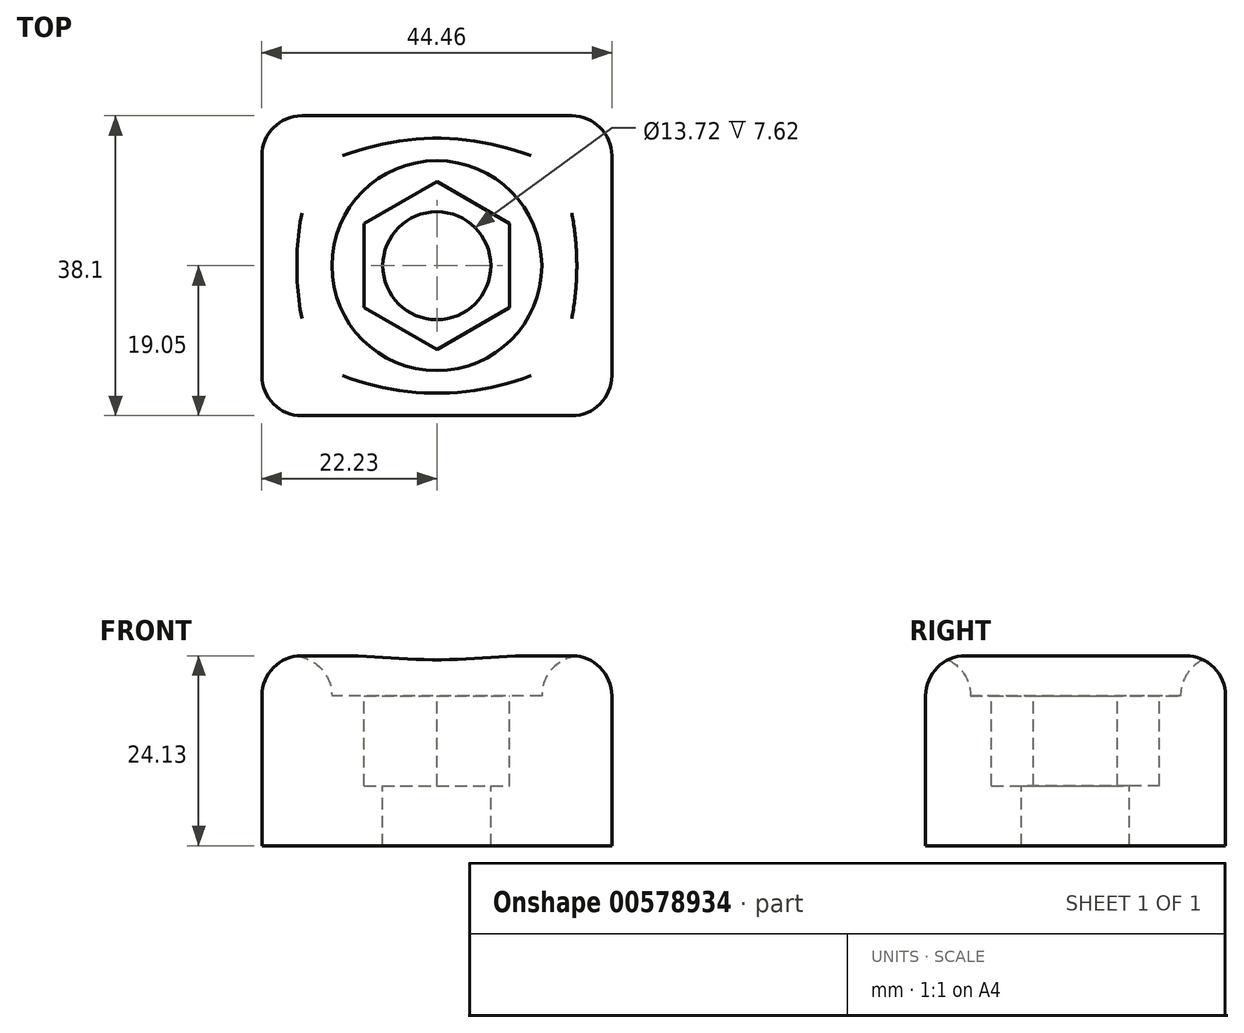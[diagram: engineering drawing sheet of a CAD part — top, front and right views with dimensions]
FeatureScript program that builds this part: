
annotation { "Feature Type Name" : "Feature", "Feature Type Description" : "" }
export const myFeature = defineFeature(function(context is Context, id is Id, definition is map)
    precondition{}
    {
        {
            var Q0;
            Q0=qCreatedBy(makeId("Top.planeOp"),FACE);
            var sketch = newSketch(context, id + "F0", { "sketchPlane" : qUnion([Q0])});
            skLineSegment(sketch, "E0.bottom", {"start": v(-22.23, 19.05) * mm, "end": v(22.23, 19.05) * mm});
            skLineSegment(sketch, "E0.top", {"start": v(-22.23, -19.05) * mm, "end": v(22.23, -19.05) * mm});
            skLineSegment(sketch, "E0.left", {"start": v(-22.23, 19.05) * mm, "end": v(-22.23, -19.05) * mm});
            skLineSegment(sketch, "E0.right", {"start": v(22.23, 19.05) * mm, "end": v(22.23, -19.05) * mm});
            skPoint(sketch, "E0.middle", {"position": v(0, 0) * mm});
            skSolve(sketch);
        }
        {
            var Q0;
            Q0=makeQuery(id+"F0.imprint","IMPRINT",FACE,{"disambiguationData":[TD([[makeQuery(id+"F0.imprint","IMPRINT",EDGE,{"derivedFrom":sQuery(id+"F0.wireOp",EDGE,"E0.bottom")}),-1.0]])]});
            extrude(context, id + "F1", {"entities" : qUnion([Q0]), "depth" : 16.5 * mm, "offsetDistance" : 25.4 * mm});
        }
        {
            var Q0;
            Q0=makeQuery(id+"F1.opExtrude","CAP_FACE",FACE,{"disambiguationData":[OSD([sQuery(id+"F0.wireOp",EDGE,"E0.bottom"),sQuery(id+"F0.wireOp",EDGE,"E0.top"),sQuery(id+"F0.wireOp",EDGE,"E0.left"),sQuery(id+"F0.wireOp",EDGE,"E0.right")])],"isStart":false});
            var sketch = newSketch(context, id + "F2", { "sketchPlane" : qUnion([Q0])});
            skCircle(sketch, "E1.cCircle", {"center": v(0, 0) * mm, "radius": 10.67 * mm, "construction": true});
            skLineSegment(sketch, "E1.0", {"start": v(0, 10.67) * mm, "end": v(9.24, 5.33) * mm});
            skLineSegment(sketch, "E1.1", {"start": v(9.24, 5.33) * mm, "end": v(9.24, -5.33) * mm});
            skLineSegment(sketch, "E1.2", {"start": v(9.24, -5.33) * mm, "end": v(0, -10.67) * mm});
            skLineSegment(sketch, "E1.3", {"start": v(0, -10.67) * mm, "end": v(-9.24, -5.33) * mm});
            skLineSegment(sketch, "E1.4", {"start": v(-9.24, -5.33) * mm, "end": v(-9.24, 5.33) * mm});
            skLineSegment(sketch, "E1.5", {"start": v(-9.24, 5.33) * mm, "end": v(0, 10.67) * mm});
            skSolve(sketch);
        }
        {
            var Q0;
            Q0=makeQuery(id+"F2.imprint","IMPRINT",FACE,{"disambiguationData":[TD([[makeQuery(id+"F2.imprint","IMPRINT",EDGE,{"derivedFrom":sQuery(id+"F2.wireOp",EDGE,"E1.0")}),-1.0]])]});
            extrude(context, id + "F3", {"entities" : qUnion([Q0]), "operationType" : NewBodyOperationType.REMOVE, "oppositeDirection" : true, "depth" : 25.4 * mm, "offsetDistance" : 25.4 * mm});
        }
        {
            var Q0;
            Q0=makeQuery(id+"F1.opExtrude","CAP_FACE",FACE,{"disambiguationData":[OSD([sQuery(id+"F0.wireOp",EDGE,"E0.bottom"),sQuery(id+"F0.wireOp",EDGE,"E0.top"),sQuery(id+"F0.wireOp",EDGE,"E0.left"),sQuery(id+"F0.wireOp",EDGE,"E0.right")])],"isStart":false});
            var sketch = newSketch(context, id + "F4", { "sketchPlane" : qUnion([Q0])});
            skCircle(sketch, "E2", {"center": v(0, 0) * mm, "radius": 13.34 * mm});
            skSolve(sketch);
        }
        {
            var Q0;
            Q0=makeQuery(id+"F4.imprint","IMPRINT",FACE,{"disambiguationData":[TD([[makeQuery(id+"F4.imprint","IMPRINT",EDGE,{"derivedFrom":sQuery(id+"F4.wireOp",EDGE,"E2")}),1.0]])]});
            extrude(context, id + "F5", {"entities" : qUnion([Q0]), "operationType" : NewBodyOperationType.REMOVE, "oppositeDirection" : true, "depth" : 5.08 * mm, "offsetDistance" : 25.4 * mm});
        }
        {
            var Q0;
            Q0=makeQuery(id+"F1.opExtrude","CAP_EDGE",EDGE,{"disambiguationData":[OSD([sQuery(id+"F0.wireOp",EDGE,"E0.bottom")])],"isStart":false});
            var Q1;
            Q1=makeQuery(id+"F1.opExtrude","CAP_EDGE",EDGE,{"disambiguationData":[OSD([sQuery(id+"F0.wireOp",EDGE,"E0.right")])],"isStart":false});
            var Q2;
            Q2=makeQuery(id+"F1.opExtrude","CAP_FACE",FACE,{"disambiguationData":[OSD([sQuery(id+"F0.wireOp",EDGE,"E0.bottom"),sQuery(id+"F0.wireOp",EDGE,"E0.top"),sQuery(id+"F0.wireOp",EDGE,"E0.left"),sQuery(id+"F0.wireOp",EDGE,"E0.right")])],"isStart":false});
            fillet(context, id + "F6", {"entities" : qUnion([Q0, Q1, Q2]), "radius" : 5.08 * mm, "tangentPropagation" : true, "allowEdgeOverflow" : false});
        }
        {
            var Q0;
            Q0=makeQuery(id+"F1.opExtrude","SWEPT_EDGE",EDGE,{"disambiguationData":[OSD([sQuery(id+"F0.wireOp",EDGE,"E0.top"),sQuery(id+"F0.wireOp",EDGE,"E0.right")])]});
            var Q1;
            Q1=makeQuery(id+"F1.opExtrude","SWEPT_EDGE",EDGE,{"disambiguationData":[OSD([sQuery(id+"F0.wireOp",EDGE,"E0.bottom"),sQuery(id+"F0.wireOp",EDGE,"E0.right")])]});
            var Q2;
            Q2=makeQuery(id+"F1.opExtrude","SWEPT_EDGE",EDGE,{"disambiguationData":[OSD([sQuery(id+"F0.wireOp",EDGE,"E0.bottom"),sQuery(id+"F0.wireOp",EDGE,"E0.left")])]});
            var Q3;
            Q3=makeQuery(id+"F1.opExtrude","SWEPT_EDGE",EDGE,{"disambiguationData":[OSD([sQuery(id+"F0.wireOp",EDGE,"E0.top"),sQuery(id+"F0.wireOp",EDGE,"E0.left")])]});
            fillet(context, id + "F7", {"entities" : qUnion([Q0, Q1, Q2, Q3]), "radius" : 5.08 * mm, "tangentPropagation" : true, "allowEdgeOverflow" : false});
        }
        {
            var Q0;
            Q0=makeQuery(id+"F1.opExtrude","CAP_FACE",FACE,{"disambiguationData":[OSD([sQuery(id+"F0.wireOp",EDGE,"E0.bottom"),sQuery(id+"F0.wireOp",EDGE,"E0.top"),sQuery(id+"F0.wireOp",EDGE,"E0.left"),sQuery(id+"F0.wireOp",EDGE,"E0.right")])],"isStart":true});
            var sketch = newSketch(context, id + "F8", { "sketchPlane" : qUnion([Q0])});
            skCircle(sketch, "E3", {"center": v(0, 0) * mm, "radius": 6.86 * mm});
            skSolve(sketch);
        }
        {
            var Q0;
            {var subQ3=sQuery(id+"F0.wireOp",EDGE,"E0.bottom");Q0=makeQuery(id+"F8.imprint","IMPRINT",FACE,{"disambiguationData":[TD([[makeQuery(id+"F8.imprint","IMPRINT",EDGE,{"derivedFrom":makeQuery(id+"F1.opExtrude","CAP_EDGE",EDGE,{"disambiguationData":[OSD([subQ3])],"isStart":true})}),1.0]])]});}
            var Q1;
            Q1=makeQuery(id+"F8.imprint","IMPRINT",FACE,{"disambiguationData":[TD([[makeQuery(id+"F8.imprint","IMPRINT",EDGE,{"derivedFrom":sQuery(id+"F8.wireOp",EDGE,"E3")}),-1.0]])]});
            extrude(context, id + "F9", {"entities" : qUnion([Q0, Q1]), "operationType" : NewBodyOperationType.ADD, "depth" : 7.62 * mm, "offsetDistance" : 25.4 * mm});
        }
    });
